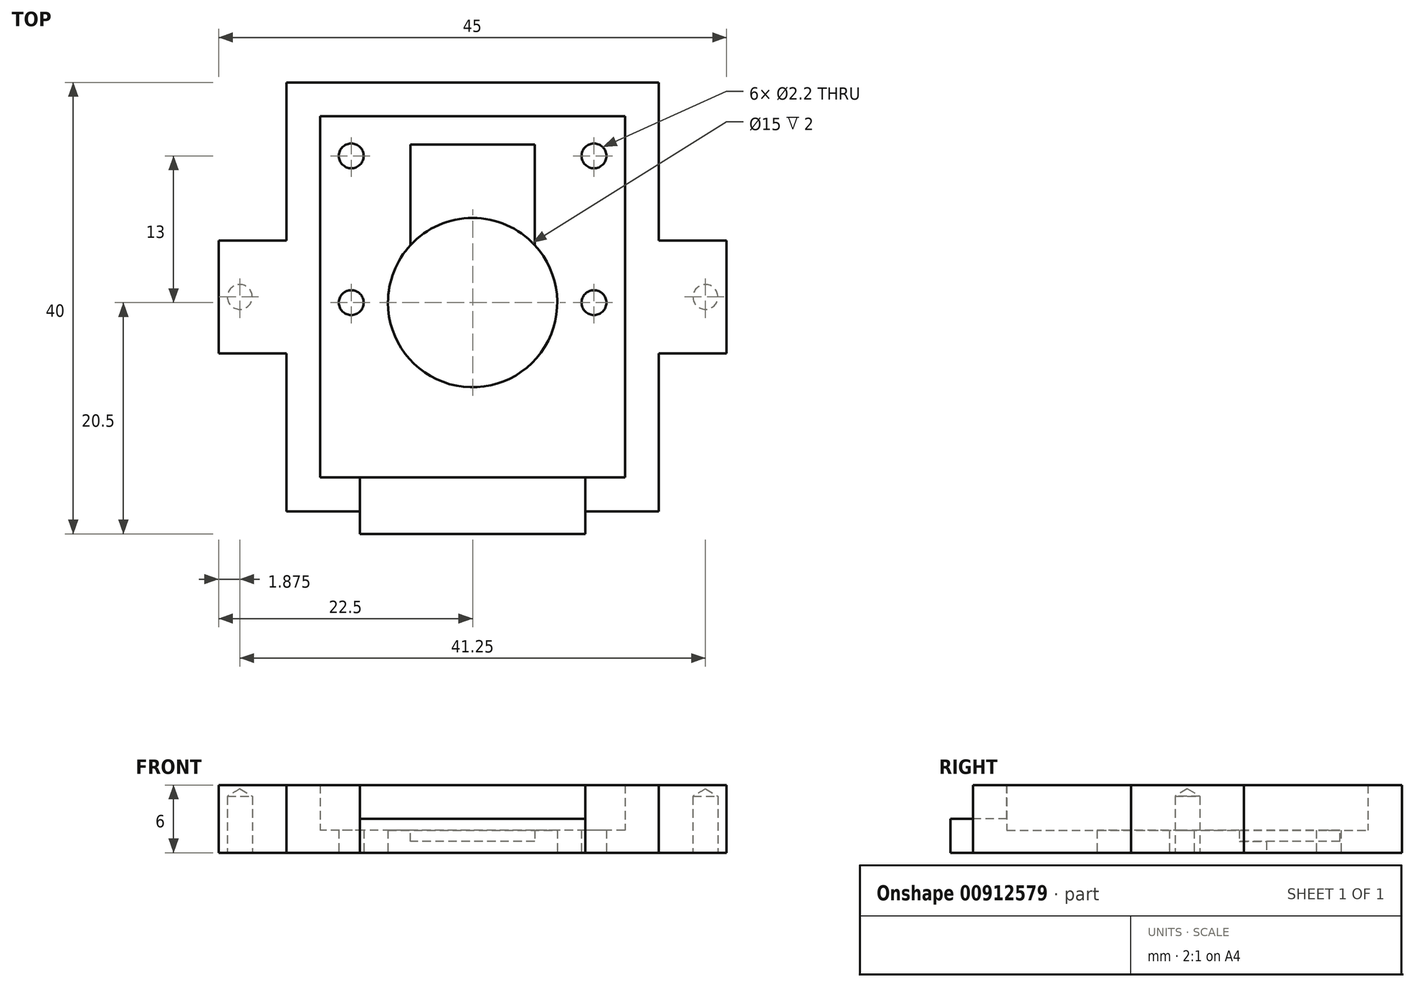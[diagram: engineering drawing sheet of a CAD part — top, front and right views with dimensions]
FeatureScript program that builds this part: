
annotation { "Feature Type Name" : "Feature", "Feature Type Description" : "" }
export const myFeature = defineFeature(function(context is Context, id is Id, definition is map)
    precondition{}
    {
        {
            var Q0;
            Q0=qCreatedBy(makeId("Top.planeOp"),FACE);
            var sketch = newSketch(context, id + "F0", { "sketchPlane" : qUnion([Q0])});
            skLineSegment(sketch, "E0.bottom", {"start": v(16.5, -19) * mm, "end": v(-16.5, -19) * mm});
            skLineSegment(sketch, "E0.top", {"start": v(16.5, 19) * mm, "end": v(-16.5, 19) * mm});
            skLineSegment(sketch, "E0.left", {"start": v(16.5, -19) * mm, "end": v(16.5, 19) * mm});
            skLineSegment(sketch, "E0.right", {"start": v(-16.5, -19) * mm, "end": v(-16.5, 19) * mm});
            skPoint(sketch, "E0.middle", {"position": v(0, 0) * mm});
            skLineSegment(sketch, "E1.bottom", {"start": v(13.5, -16) * mm, "end": v(-13.5, -16) * mm});
            skLineSegment(sketch, "E1.top", {"start": v(13.5, 16) * mm, "end": v(-13.5, 16) * mm});
            skLineSegment(sketch, "E1.left", {"start": v(13.5, -16) * mm, "end": v(13.5, 16) * mm});
            skLineSegment(sketch, "E1.right", {"start": v(-13.5, -16) * mm, "end": v(-13.5, 16) * mm});
            skLineSegment(sketch, "E2.bottom", {"start": v(114.45, -23.32) * mm, "end": v(77.2, -23.32) * mm});
            skLineSegment(sketch, "E2.top", {"start": v(114.45, 18.93) * mm, "end": v(77.2, 18.93) * mm});
            skLineSegment(sketch, "E2.left", {"start": v(114.45, -23.32) * mm, "end": v(114.45, 18.93) * mm});
            skLineSegment(sketch, "E2.right", {"start": v(77.2, -23.32) * mm, "end": v(77.2, 18.93) * mm});
            skPoint(sketch, "E2.middle", {"position": v(95.82, -2.2) * mm});
            skLineSegment(sketch, "E3.bottom", {"start": v(112.45, -21.32) * mm, "end": v(79.2, -21.32) * mm});
            skLineSegment(sketch, "E3.top", {"start": v(112.45, 16.93) * mm, "end": v(79.2, 16.93) * mm});
            skLineSegment(sketch, "E3.left", {"start": v(112.45, -21.32) * mm, "end": v(112.45, 16.93) * mm});
            skLineSegment(sketch, "E3.right", {"start": v(79.2, -21.32) * mm, "end": v(79.2, 16.93) * mm});
            skSolve(sketch);
        }
        {
            var Q0;
            Q0=makeQuery(id+"F0.imprint","IMPRINT",FACE,{"disambiguationData":[TD([[makeQuery(id+"F0.imprint","IMPRINT",EDGE,{"derivedFrom":sQuery(id+"F0.wireOp",EDGE,"E0.bottom")}),-1.0]])]});
            extrude(context, id + "F1", {"entities" : qUnion([Q0]), "depth" : 6 * mm, "offsetDistance" : 25 * mm});
        }
        {
            var Q0;
            Q0=makeQuery(id+"F0.imprint","IMPRINT",FACE,{"disambiguationData":[TD([[makeQuery(id+"F0.imprint","IMPRINT",EDGE,{"derivedFrom":sQuery(id+"F0.wireOp",EDGE,"E1.bottom")}),-1.0]])]});
            extrude(context, id + "F2", {"entities" : qUnion([Q0]), "operationType" : NewBodyOperationType.ADD, "depth" : 2 * mm, "offsetDistance" : 25 * mm});
        }
        {
            var Q0;
            {var subQ0=sQuery(id+"F0.wireOp",EDGE,"E1.right");var subQ1=sQuery(id+"F0.wireOp",EDGE,"E1.left");var subQ2=sQuery(id+"F0.wireOp",EDGE,"E1.top");var subQ3=sQuery(id+"F0.wireOp",EDGE,"E1.bottom");Q0=makeQuery(id+"F2.boolean.opBoolean","MERGE",FACE,{"derivedFrom":[makeQuery(id+"F1.opExtrude","CAP_FACE",FACE,{"disambiguationData":[OSD([sQuery(id+"F0.wireOp",EDGE,"E0.bottom"),sQuery(id+"F0.wireOp",EDGE,"E0.top"),sQuery(id+"F0.wireOp",EDGE,"E0.left"),sQuery(id+"F0.wireOp",EDGE,"E0.right"),subQ3,subQ2,subQ1,subQ0])],"isStart":true}),makeQuery(id+"F2.opExtrude","CAP_FACE",FACE,{"disambiguationData":[OSD([subQ3,subQ2,subQ1,subQ0])],"isStart":true})]});}
            var sketch = newSketch(context, id + "F3", { "sketchPlane" : qUnion([Q0])});
            skPoint(sketch, "E4", {"position": v(0, 0.5) * mm});
            skPoint(sketch, "E5", {"position": v(16.5, 0.5) * mm});
            skPoint(sketch, "E6", {"position": v(-16.5, 0.5) * mm});
            skPoint(sketch, "E7", {"position": v(-10.75, -12.5) * mm});
            skPoint(sketch, "E8", {"position": v(-10.75, 0.5) * mm});
            skPoint(sketch, "E9", {"position": v(10.75, 0.5) * mm});
            skPoint(sketch, "E10", {"position": v(10.75, -12.5) * mm});
            skCircle(sketch, "E11", {"center": v(0, 0.5) * mm, "radius": 7.5 * mm});
            skSolve(sketch);
        }
        {
            var Q0;
            Q0=sQuery(id+"F3.wireOp",VERTEX,"E8");
            var Q1;
            Q1=sQuery(id+"F3.wireOp",VERTEX,"E7");
            var Q2;
            Q2=sQuery(id+"F3.wireOp",VERTEX,"E10");
            var Q3;
            Q3=sQuery(id+"F3.wireOp",VERTEX,"E9");
            var Q4;
            Q4=makeQuery(id+"F1.opExtrude","SWEPT_BODY",BODY,{"disambiguationData":[OSD([sQuery(id+"F0.wireOp",EDGE,"E0.bottom"),sQuery(id+"F0.wireOp",EDGE,"E0.top"),sQuery(id+"F0.wireOp",EDGE,"E0.left"),sQuery(id+"F0.wireOp",EDGE,"E0.right"),sQuery(id+"F0.wireOp",EDGE,"E1.bottom"),sQuery(id+"F0.wireOp",EDGE,"E1.top"),sQuery(id+"F0.wireOp",EDGE,"E1.left"),sQuery(id+"F0.wireOp",EDGE,"E1.right")])]});
            hole(context, id + "F4", {"style" : HoleStyle.SIMPLE, "endStyle" : HoleEndStyle.BLIND, "holeDiameter" : 2.2 * mm, "majorDiameter" : 5 * mm, "holeDepth" : 5 * mm, "isTappedThrough" : true, "tappedDepth" : 12 * mm, "tapClearance" : 3, "locations" : qUnion([Q0, Q1, Q2, Q3]), "scope" : qUnion([Q4])});
        }
        {
            var Q0;
            Q0=makeQuery(id+"F1.opExtrude","SWEPT_FACE",FACE,{"disambiguationData":[OSD([sQuery(id+"F0.wireOp",EDGE,"E0.left")])]});
            var sketch = newSketch(context, id + "F5", { "sketchPlane" : qUnion([Q0])});
            skLineSegment(sketch, "E12.bottom", {"start": v(-5, 0) * mm, "end": v(5, 0) * mm});
            skLineSegment(sketch, "E12.top", {"start": v(-5, 6) * mm, "end": v(5, 6) * mm});
            skLineSegment(sketch, "E12.left", {"start": v(-5, 0) * mm, "end": v(-5, 6) * mm});
            skLineSegment(sketch, "E12.right", {"start": v(5, 0) * mm, "end": v(5, 6) * mm});
            skSolve(sketch);
        }
        {
            var Q0;
            Q0=makeQuery(id+"F5.imprint","IMPRINT",FACE,{"disambiguationData":[TD([[makeQuery(id+"F5.imprint","IMPRINT",EDGE,{"derivedFrom":sQuery(id+"F5.wireOp",EDGE,"E12.bottom")}),1.0]])]});
            extrude(context, id + "F6", {"entities" : qUnion([Q0]), "operationType" : NewBodyOperationType.ADD, "depth" : 6 * mm, "offsetDistance" : 25 * mm});
        }
        {
            var Q0;
            Q0=makeQuery(id+"F1.opExtrude","SWEPT_FACE",FACE,{"disambiguationData":[OSD([sQuery(id+"F0.wireOp",EDGE,"E0.right")])]});
            var sketch = newSketch(context, id + "F7", { "sketchPlane" : qUnion([Q0])});
            skLineSegment(sketch, "E13.bottom", {"start": v(-5, 6) * mm, "end": v(5, 6) * mm});
            skLineSegment(sketch, "E13.top", {"start": v(-5, 0) * mm, "end": v(5, 0) * mm});
            skLineSegment(sketch, "E13.left", {"start": v(-5, 6) * mm, "end": v(-5, 0) * mm});
            skLineSegment(sketch, "E13.right", {"start": v(5, 6) * mm, "end": v(5, 0) * mm});
            skSolve(sketch);
        }
        {
            var Q0;
            Q0=makeQuery(id+"F7.imprint","IMPRINT",FACE,{"disambiguationData":[TD([[makeQuery(id+"F7.imprint","IMPRINT",EDGE,{"derivedFrom":sQuery(id+"F7.wireOp",EDGE,"E13.bottom")}),1.0]])]});
            extrude(context, id + "F8", {"entities" : qUnion([Q0]), "operationType" : NewBodyOperationType.ADD, "depth" : 6 * mm, "offsetDistance" : 25 * mm});
        }
        {
            var Q0;
            {var subQ0=sQuery(id+"F0.wireOp",EDGE,"E1.right");var subQ1=sQuery(id+"F0.wireOp",EDGE,"E1.left");var subQ2=sQuery(id+"F0.wireOp",EDGE,"E1.top");var subQ3=sQuery(id+"F0.wireOp",EDGE,"E1.bottom");Q0=makeQuery(id+"F8.boolean.opBoolean","MERGE",FACE,{"derivedFrom":[makeQuery(id+"F6.boolean.opBoolean","MERGE",FACE,{"derivedFrom":[makeQuery(id+"F2.boolean.opBoolean","MERGE",FACE,{"derivedFrom":[makeQuery(id+"F1.opExtrude","CAP_FACE",FACE,{"disambiguationData":[OSD([sQuery(id+"F0.wireOp",EDGE,"E0.bottom"),sQuery(id+"F0.wireOp",EDGE,"E0.top"),sQuery(id+"F0.wireOp",EDGE,"E0.left"),sQuery(id+"F0.wireOp",EDGE,"E0.right"),subQ3,subQ2,subQ1,subQ0])],"isStart":true}),makeQuery(id+"F2.opExtrude","CAP_FACE",FACE,{"disambiguationData":[OSD([subQ3,subQ2,subQ1,subQ0])],"isStart":true})]}),makeQuery(id+"F6.opExtrude","SWEPT_FACE",FACE,{"disambiguationData":[OSD([sQuery(id+"F5.wireOp",EDGE,"E12.bottom")])]})]}),makeQuery(id+"F8.opExtrude","SWEPT_FACE",FACE,{"disambiguationData":[OSD([sQuery(id+"F7.wireOp",EDGE,"E13.top")])]})]});}
            var sketch = newSketch(context, id + "F9", { "sketchPlane" : qUnion([Q0])});
            skPoint(sketch, "E14", {"position": v(20.62, 0) * mm});
            skPoint(sketch, "E14.positionSnap0", {"position": v(22.5, 0) * mm});
            skPoint(sketch, "E15", {"position": v(-20.62, 0) * mm});
            skPoint(sketch, "E15.positionSnap0", {"position": v(-22.5, 0) * mm});
            skSolve(sketch);
        }
        {
            var Q0;
            Q0=sQuery(id+"F9.wireOp",VERTEX,"E14");
            var Q1;
            Q1=sQuery(id+"F9.wireOp",VERTEX,"E15");
            var Q2;
            Q2=makeQuery(id+"F1.opExtrude","SWEPT_BODY",BODY,{"disambiguationData":[OSD([sQuery(id+"F0.wireOp",EDGE,"E0.bottom"),sQuery(id+"F0.wireOp",EDGE,"E0.top"),sQuery(id+"F0.wireOp",EDGE,"E0.left"),sQuery(id+"F0.wireOp",EDGE,"E0.right"),sQuery(id+"F0.wireOp",EDGE,"E1.bottom"),sQuery(id+"F0.wireOp",EDGE,"E1.top"),sQuery(id+"F0.wireOp",EDGE,"E1.left"),sQuery(id+"F0.wireOp",EDGE,"E1.right")])]});
            hole(context, id + "F10", {"style" : HoleStyle.SIMPLE, "endStyle" : HoleEndStyle.BLIND, "holeDiameter" : 2.2 * mm, "majorDiameter" : 5 * mm, "holeDepth" : 5 * mm, "isTappedThrough" : true, "tappedDepth" : 12 * mm, "tapClearance" : 3, "locations" : qUnion([Q0, Q1]), "scope" : qUnion([Q2])});
        }
        {
            var Q0;
            Q0=makeQuery(id+"F1.opExtrude","SWEPT_FACE",FACE,{"disambiguationData":[OSD([sQuery(id+"F0.wireOp",EDGE,"E0.bottom")])]});
            var sketch = newSketch(context, id + "F11", { "sketchPlane" : qUnion([Q0])});
            skLineSegment(sketch, "E16.bottom", {"start": v(10, 6) * mm, "end": v(-10, 6) * mm});
            skLineSegment(sketch, "E16.top", {"start": v(10, 3) * mm, "end": v(-10, 3) * mm});
            skLineSegment(sketch, "E16.left", {"start": v(10, 6) * mm, "end": v(10, 3) * mm});
            skLineSegment(sketch, "E16.right", {"start": v(-10, 6) * mm, "end": v(-10, 3) * mm});
            skSolve(sketch);
        }
        {
            var Q0;
            Q0=makeQuery(id+"F11.imprint","IMPRINT",FACE,{"disambiguationData":[TD([[makeQuery(id+"F11.imprint","IMPRINT",EDGE,{"derivedFrom":sQuery(id+"F11.wireOp",EDGE,"E16.bottom")}),1.0]])]});
            extrude(context, id + "F12", {"entities" : qUnion([Q0]), "operationType" : NewBodyOperationType.REMOVE, "endBound" : BoundingType.UP_TO_NEXT, "oppositeDirection" : true, "depth" : 25 * mm, "offsetDistance" : 25 * mm});
        }
        {
            var Q0;
            Q0=makeQuery(id+"F1.opExtrude","SWEPT_FACE",FACE,{"disambiguationData":[OSD([sQuery(id+"F0.wireOp",EDGE,"E0.bottom")])]});
            var sketch = newSketch(context, id + "F13", { "sketchPlane" : qUnion([Q0])});
            skLineSegment(sketch, "E17", {"start": v(10, 3) * mm, "end": v(10, 0) * mm});
            skLineSegment(sketch, "E18", {"start": v(-10, 3) * mm, "end": v(-10, 0) * mm});
            skSolve(sketch);
        }
        {
            var Q0;
            {var subQ0=sQuery(id+"F13.wireOp",EDGE,"E17");Q0=makeQuery(id+"F13.imprint","IMPRINT",FACE,{"disambiguationData":[TD([[makeQuery(id+"F13.imprint","IMPRINT",EDGE,{"derivedFrom":subQ0}),-1.0]])]});}
            extrude(context, id + "F14", {"entities" : qUnion([Q0]), "operationType" : NewBodyOperationType.ADD, "depth" : 2 * mm, "offsetDistance" : 25 * mm});
        }
        {
            var Q0;
            {var subQ0=sQuery(id+"F11.wireOp",EDGE,"E16.top");Q0=makeQuery(id+"F14.boolean.opBoolean","MERGE",FACE,{"derivedFrom":[makeQuery(id+"F12.boolean.opBoolean","MERGE",FACE,{"derivedFrom":[makeQuery(id+"F2.opExtrude","CAP_FACE",FACE,{"disambiguationData":[OSD([sQuery(id+"F0.wireOp",EDGE,"E1.bottom"),sQuery(id+"F0.wireOp",EDGE,"E1.top"),sQuery(id+"F0.wireOp",EDGE,"E1.left"),sQuery(id+"F0.wireOp",EDGE,"E1.right")])],"isStart":false})],"fromTools":[makeQuery(id+"F12.opExtrude","SWEPT_FACE",FACE,{"disambiguationData":[OSD([subQ0])]})]}),makeQuery(id+"F14.opExtrude","SWEPT_FACE",FACE,{"disambiguationData":[OSD([subQ0])]})]});}
            var sketch = newSketch(context, id + "F15", { "sketchPlane" : qUnion([Q0])});
            skLineSegment(sketch, "E19.bottom", {"start": v(5.5, 13.5) * mm, "end": v(-5.5, 13.5) * mm});
            skLineSegment(sketch, "E19.top", {"start": v(5.5, -1.5) * mm, "end": v(-5.5, -1.5) * mm});
            skLineSegment(sketch, "E19.left", {"start": v(5.5, 13.5) * mm, "end": v(5.5, -1.5) * mm});
            skLineSegment(sketch, "E19.right", {"start": v(-5.5, 13.5) * mm, "end": v(-5.5, -1.5) * mm});
            skPoint(sketch, "E19.middle", {"position": v(0, 6) * mm});
            skSolve(sketch);
        }
        {
            var Q0;
            {var subQ0=sQuery(id+"F15.wireOp",EDGE,"E19.bottom");Q0=makeQuery(id+"F15.imprint","IMPRINT",FACE,{"disambiguationData":[TD([[makeQuery(id+"F15.imprint","IMPRINT",EDGE,{"derivedFrom":subQ0}),1.0]])]});}
            extrude(context, id + "F16", {"entities" : qUnion([Q0]), "operationType" : NewBodyOperationType.REMOVE, "oppositeDirection" : true, "depth" : 2 * mm, "offsetDistance" : 25 * mm});
        }
        {
            var Q0;
            Q0=makeQuery(id+"F3.imprint","IMPRINT",FACE,{"disambiguationData":[TD([[makeQuery(id+"F3.imprint","IMPRINT",EDGE,{"derivedFrom":sQuery(id+"F3.wireOp",EDGE,"E11")}),1.0]])]});
            extrude(context, id + "F17", {"entities" : qUnion([Q0]), "operationType" : NewBodyOperationType.REMOVE, "endBound" : BoundingType.UP_TO_NEXT, "oppositeDirection" : true, "depth" : 25 * mm, "offsetDistance" : 25 * mm});
        }
    });
